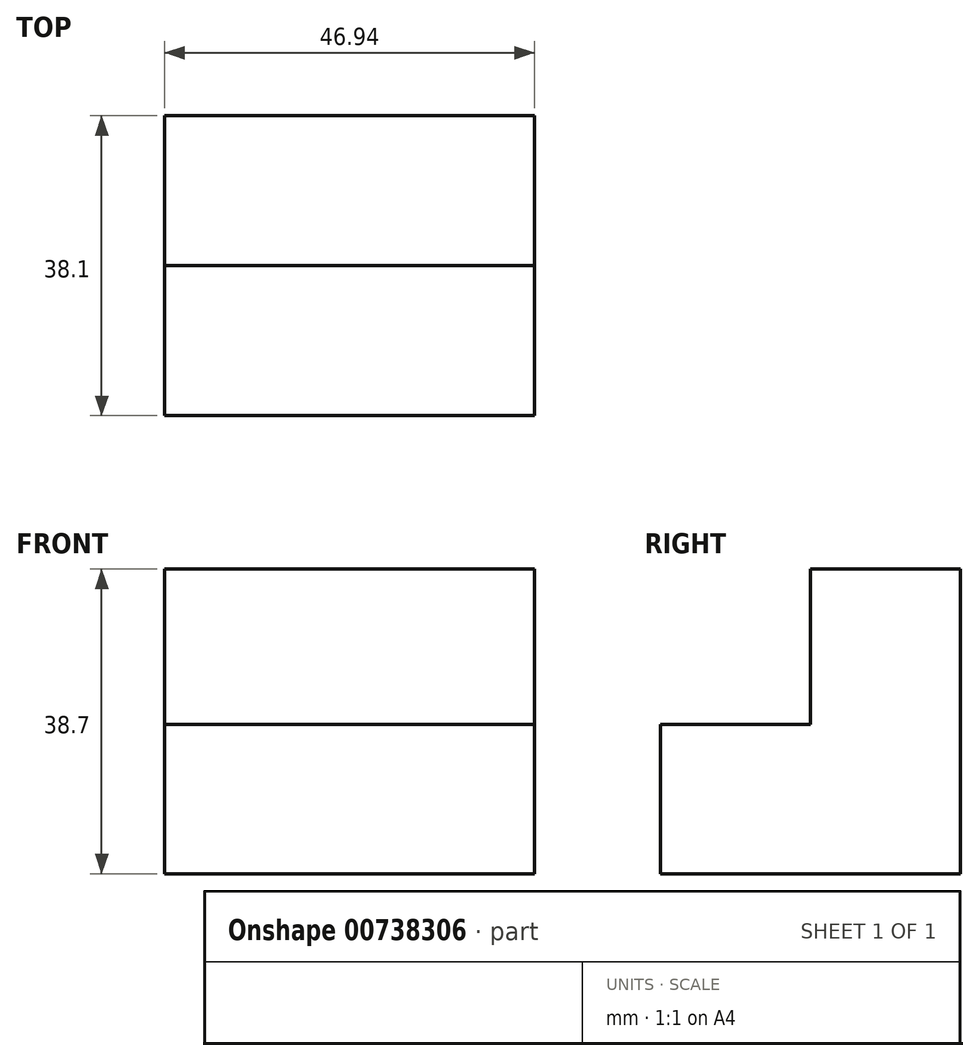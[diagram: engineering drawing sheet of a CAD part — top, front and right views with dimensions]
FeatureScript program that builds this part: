
annotation { "Feature Type Name" : "Feature", "Feature Type Description" : "" }
export const myFeature = defineFeature(function(context is Context, id is Id, definition is map)
    precondition{}
    {
        {
            var Q0;
            Q0=qCreatedBy(makeId("Front.planeOp"),FACE);
            var sketch = newSketch(context, id + "F0", { "sketchPlane" : qUnion([Q0])});
            skLineSegment(sketch, "E0", {"start": v(0, 0) * mm, "end": v(0, 38.7) * mm});
            skLineSegment(sketch, "E1", {"start": v(0, 38.7) * mm, "end": v(46.94, 38.7) * mm});
            skLineSegment(sketch, "E2", {"start": v(46.94, 38.7) * mm, "end": v(46.94, 0) * mm});
            skLineSegment(sketch, "E3", {"start": v(46.94, 0) * mm, "end": v(0, 0) * mm});
            skSolve(sketch);
        }
        {
            var Q0;
            Q0=makeQuery(id+"F0.imprint","IMPRINT",FACE,{"disambiguationData":[TD([[makeQuery(id+"F0.imprint","IMPRINT",EDGE,{"derivedFrom":sQuery(id+"F0.wireOp",EDGE,"E0")}),-1.0]])]});
            extrude(context, id + "F1", {"entities" : qUnion([Q0]), "depth" : 38.1 * mm, "offsetDistance" : 25.4 * mm});
        }
        {
            var Q0;
            Q0=makeQuery(id+"F1.opExtrude","SWEPT_FACE",FACE,{"disambiguationData":[OSD([sQuery(id+"F0.wireOp",EDGE,"E2")])]});
            var sketch = newSketch(context, id + "F2", { "sketchPlane" : qUnion([Q0])});
            skLineSegment(sketch, "E4", {"start": v(-19.05, 38.7) * mm, "end": v(-19.05, 19.2) * mm});
            skLineSegment(sketch, "E5", {"start": v(-19.05, 19.2) * mm, "end": v(-38.1, 19.2) * mm});
            skSolve(sketch);
        }
        {
            var Q0;
            Q0=makeQuery(id+"F1.opExtrude","SWEPT_FACE",FACE,{"disambiguationData":[OSD([sQuery(id+"F0.wireOp",EDGE,"E0")])]});
            var sketch = newSketch(context, id + "F3", { "sketchPlane" : qUnion([Q0])});
            skLineSegment(sketch, "E6", {"start": v(19.05, 38.7) * mm, "end": v(19.05, 19) * mm});
            skLineSegment(sketch, "E7", {"start": v(19.05, 19) * mm, "end": v(38.1, 19) * mm});
            skSolve(sketch);
        }
        {
            var Q0;
            {var subQ0=sQuery(id+"F3.wireOp",EDGE,"E6");Q0=makeQuery(id+"F3.imprint","IMPRINT",FACE,{"disambiguationData":[TD([[makeQuery(id+"F3.imprint","IMPRINT",EDGE,{"derivedFrom":subQ0}),1.0]])]});}
            extrude(context, id + "F4", {"entities" : qUnion([Q0]), "operationType" : NewBodyOperationType.REMOVE, "oppositeDirection" : true, "depth" : 25.4 * mm, "offsetDistance" : 25.4 * mm});
        }
        {
            var Q0;
            Q0=makeQuery(id+"F4.boolean.opBoolean","COPY",FACE,{"derivedFrom":makeQuery(id+"F4.opExtrude","CAP_FACE",FACE,{"disambiguationData":[OSD([sQuery(id+"F0.wireOp",EDGE,"E0"),sQuery(id+"F0.wireOp",EDGE,"E1"),sQuery(id+"F3.wireOp",EDGE,"E6"),sQuery(id+"F3.wireOp",EDGE,"E7")])],"isStart":false})});
            extrude(context, id + "F5", {"entities" : qUnion([Q0]), "operationType" : NewBodyOperationType.REMOVE, "oppositeDirection" : true, "depth" : 50.8 * mm, "offsetDistance" : 25.4 * mm});
        }
    });
